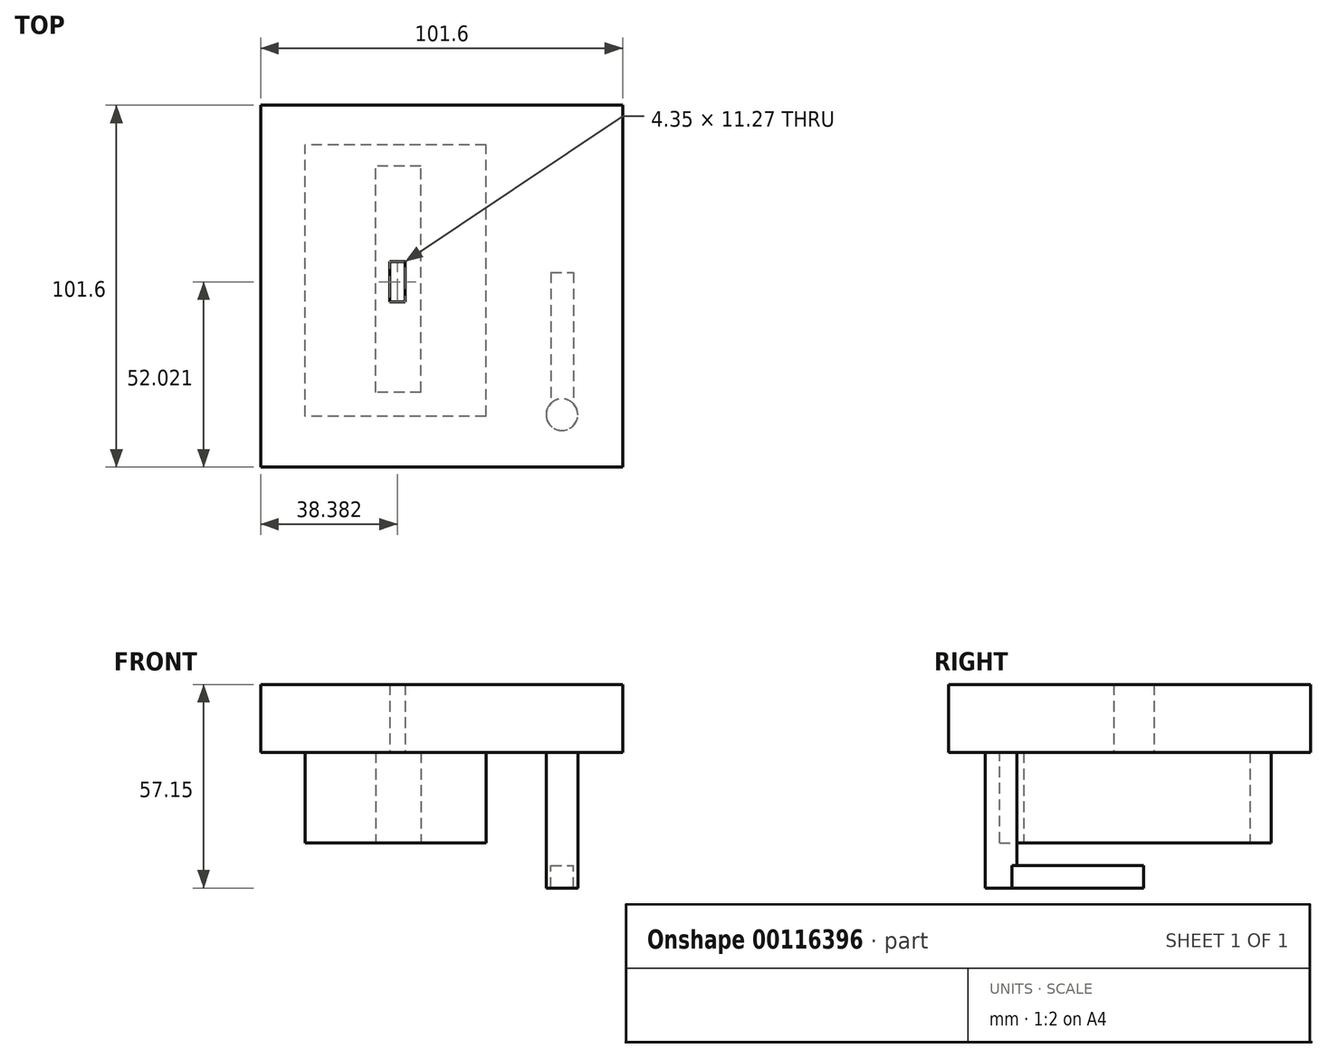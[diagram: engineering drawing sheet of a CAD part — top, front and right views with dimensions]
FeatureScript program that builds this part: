
annotation { "Feature Type Name" : "Feature", "Feature Type Description" : "" }
export const myFeature = defineFeature(function(context is Context, id is Id, definition is map)
    precondition{}
    {
        {
            var Q0;
            Q0=qCreatedBy(makeId("Top.planeOp"),FACE);
            cPlane(context, id + "F0", {"entities" : qUnion([Q0]), "cplaneType" : CPlaneType.OFFSET, "offset" : 25.4 * mm, "width" : 152.4 * mm, "height" : 152.4 * mm});
        }
        {
            var Q0;
            Q0=qCreatedBy(id+"F0.planeOp",FACE);
            var sketch = newSketch(context, id + "F1", { "sketchPlane" : qUnion([Q0])});
            skLineSegment(sketch, "E0.bottom", {"start": v(50.18, 54.16) * mm, "end": v(-51.42, 54.16) * mm});
            skLineSegment(sketch, "E0.top", {"start": v(50.18, -47.44) * mm, "end": v(-51.42, -47.44) * mm});
            skLineSegment(sketch, "E0.left", {"start": v(50.18, 54.16) * mm, "end": v(50.18, -47.44) * mm});
            skLineSegment(sketch, "E0.right", {"start": v(-51.42, 54.16) * mm, "end": v(-51.42, -47.44) * mm});
            skSolve(sketch);
        }
        {
            var Q0;
            Q0=makeQuery(id+"F1.imprint","IMPRINT",FACE,{"disambiguationData":[TD([[makeQuery(id+"F1.imprint","IMPRINT",EDGE,{"derivedFrom":sQuery(id+"F1.wireOp",EDGE,"E0.bottom")}),1.0]])]});
            extrude(context, id + "F2", {"entities" : qUnion([Q0]), "depth" : 19.05 * mm});
        }
        {
            var Q0;
            Q0=makeQuery(id+"F2.opExtrude","CAP_FACE",FACE,{"disambiguationData":[OSD([sQuery(id+"F1.wireOp",EDGE,"E0.bottom"),sQuery(id+"F1.wireOp",EDGE,"E0.top"),sQuery(id+"F1.wireOp",EDGE,"E0.left"),sQuery(id+"F1.wireOp",EDGE,"E0.right")])],"isStart":true});
            var sketch = newSketch(context, id + "F3", { "sketchPlane" : qUnion([Q0])});
            skCircle(sketch, "E1", {"center": v(33.15, 32.69) * mm, "radius": 4.45 * mm});
            skSolve(sketch);
        }
        {
            var Q0;
            Q0=makeQuery(id+"F3.imprint","IMPRINT",FACE,{"disambiguationData":[TD([[makeQuery(id+"F3.imprint","IMPRINT",EDGE,{"derivedFrom":sQuery(id+"F3.wireOp",EDGE,"E1")}),1.0]])]});
            var Q1;
            Q1=sQuery(id+"F3.wireOp",EDGE,"E1");
            extrude(context, id + "F4", {"entities" : qUnion([Q0]), "surfaceEntities" : qUnion([Q1]), "depth" : 38.1 * mm});
        }
        {
            var Q0;
            Q0=makeQuery(id+"F4.opExtrude","CAP_FACE",FACE,{"disambiguationData":[OSD([sQuery(id+"F3.wireOp",EDGE,"E1")])],"isStart":false});
            var sketch = newSketch(context, id + "F5", { "sketchPlane" : qUnion([Q0])});
            skLineSegment(sketch, "E2.bottom", {"start": v(30.05, -7.28) * mm, "end": v(36.4, -7.28) * mm});
            skLineSegment(sketch, "E2.top", {"start": v(30.05, 30.82) * mm, "end": v(36.4, 30.82) * mm});
            skLineSegment(sketch, "E2.left", {"start": v(30.05, -7.28) * mm, "end": v(30.05, 30.82) * mm});
            skLineSegment(sketch, "E2.right", {"start": v(36.4, -7.28) * mm, "end": v(36.4, 30.82) * mm});
            skSolve(sketch);
        }
        {
            var Q0;
            Q0 = qSketchRegion(id + "F5", true);
            extrude(context, id + "F6", {"entities" : qUnion([Q0]), "operationType" : NewBodyOperationType.ADD, "oppositeDirection" : true, "depth" : 6.35 * mm});
        }
        {
            var Q0;
            Q0=makeQuery(id+"F2.opExtrude","CAP_FACE",FACE,{"disambiguationData":[OSD([sQuery(id+"F1.wireOp",EDGE,"E0.bottom"),sQuery(id+"F1.wireOp",EDGE,"E0.top"),sQuery(id+"F1.wireOp",EDGE,"E0.left"),sQuery(id+"F1.wireOp",EDGE,"E0.right")])],"isStart":true});
            var sketch = newSketch(context, id + "F7", { "sketchPlane" : qUnion([Q0])});
            skLineSegment(sketch, "E3.bottom", {"start": v(11.83, 33.13) * mm, "end": v(-38.97, 33.13) * mm});
            skLineSegment(sketch, "E3.top", {"start": v(11.83, -43.07) * mm, "end": v(-38.97, -43.07) * mm});
            skLineSegment(sketch, "E3.left", {"start": v(11.83, 33.13) * mm, "end": v(11.83, -43.07) * mm});
            skLineSegment(sketch, "E3.right", {"start": v(-38.97, 33.13) * mm, "end": v(-38.97, -43.07) * mm});
            skSolve(sketch);
        }
        {
            var Q0;
            Q0 = qSketchRegion(id + "F7", true);
            extrude(context, id + "F8", {"entities" : qUnion([Q0]), "operationType" : NewBodyOperationType.ADD, "depth" : 25.4 * mm});
        }
        {
            var Q0;
            Q0=makeQuery(id+"F8.opExtrude","CAP_FACE",FACE,{"disambiguationData":[OSD([sQuery(id+"F7.wireOp",EDGE,"E3.bottom"),sQuery(id+"F7.wireOp",EDGE,"E3.top"),sQuery(id+"F7.wireOp",EDGE,"E3.left"),sQuery(id+"F7.wireOp",EDGE,"E3.right")])],"isStart":false});
            var sketch = newSketch(context, id + "F9", { "sketchPlane" : qUnion([Q0])});
            skLineSegment(sketch, "E4.bottom", {"start": v(-6.45, 26.4) * mm, "end": v(-19.15, 26.4) * mm});
            skLineSegment(sketch, "E4.top", {"start": v(-6.45, -37.1) * mm, "end": v(-19.15, -37.1) * mm});
            skLineSegment(sketch, "E4.left", {"start": v(-6.45, 26.4) * mm, "end": v(-6.45, -37.1) * mm});
            skLineSegment(sketch, "E4.right", {"start": v(-19.15, 26.4) * mm, "end": v(-19.15, -37.1) * mm});
            skSolve(sketch);
        }
        {
            var Q0;
            Q0 = qSketchRegion(id + "F9", true);
            extrude(context, id + "F10", {"entities" : qUnion([Q0]), "operationType" : NewBodyOperationType.REMOVE, "oppositeDirection" : true, "depth" : 25.4 * mm});
        }
        {
            var Q0;
            Q0=makeQuery(id+"F10.boolean.opBoolean","COPY",FACE,{"derivedFrom":makeQuery(id+"F10.opExtrude","CAP_FACE",FACE,{"disambiguationData":[OSD([sQuery(id+"F9.wireOp",EDGE,"E4.bottom"),sQuery(id+"F9.wireOp",EDGE,"E4.top"),sQuery(id+"F9.wireOp",EDGE,"E4.left"),sQuery(id+"F9.wireOp",EDGE,"E4.right")])],"isStart":false})});
            var sketch = newSketch(context, id + "F11", { "sketchPlane" : qUnion([Q0])});
            skLineSegment(sketch, "E5.bottom", {"start": v(-15.21, -10.22) * mm, "end": v(-10.86, -10.22) * mm});
            skLineSegment(sketch, "E5.top", {"start": v(-15.21, 1.05) * mm, "end": v(-10.86, 1.05) * mm});
            skLineSegment(sketch, "E5.left", {"start": v(-15.21, -10.22) * mm, "end": v(-15.21, 1.05) * mm});
            skLineSegment(sketch, "E5.right", {"start": v(-10.86, -10.22) * mm, "end": v(-10.86, 1.05) * mm});
            skSolve(sketch);
        }
        {
            var Q0;
            Q0 = qSketchRegion(id + "F11", true);
            extrude(context, id + "F12", {"entities" : qUnion([Q0]), "operationType" : NewBodyOperationType.REMOVE, "oppositeDirection" : true, "depth" : 25.4 * mm});
        }
    });
